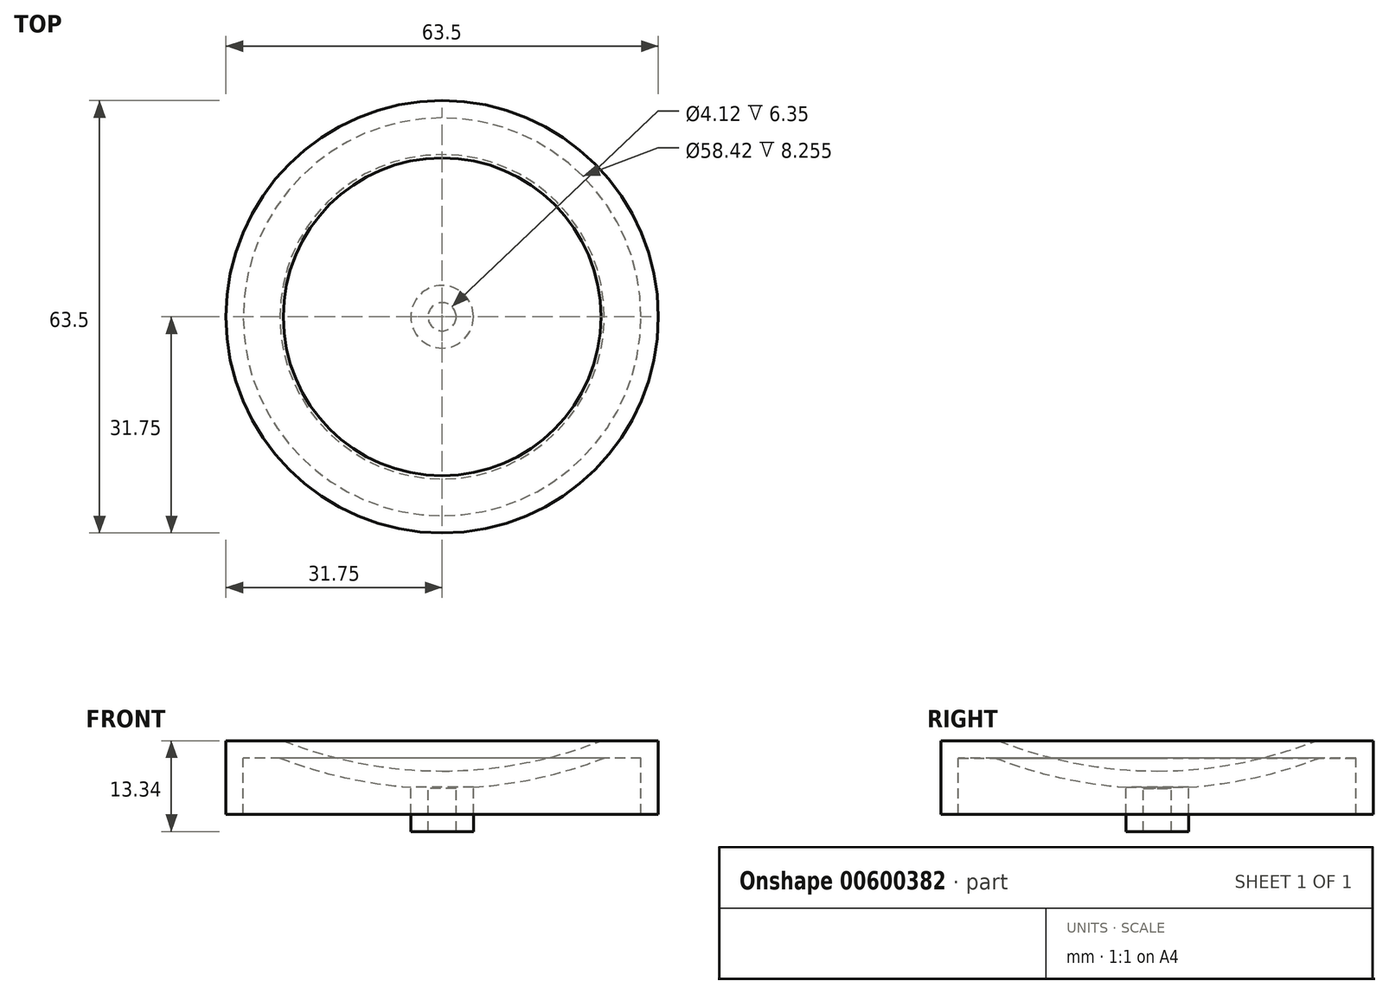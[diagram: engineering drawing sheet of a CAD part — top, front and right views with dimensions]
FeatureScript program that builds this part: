
annotation { "Feature Type Name" : "Feature", "Feature Type Description" : "" }
export const myFeature = defineFeature(function(context is Context, id is Id, definition is map)
    precondition{}
    {
        {
            var Q0;
            Q0=qCreatedBy(makeId("Front.planeOp"),FACE);
            var sketch = newSketch(context, id + "F0", { "sketchPlane" : qUnion([Q0])});
            skCircle(sketch, "E0", {"center": v(0, 59.06) * mm, "radius": 63.5 * mm, "construction": true});
            skLineSegment(sketch, "E1", {"start": v(0, -4.44) * mm, "end": v(0, -6.98) * mm});
            skLineSegment(sketch, "E2", {"start": v(0, -6.98) * mm, "end": v(2.06, -6.98) * mm});
            skLineSegment(sketch, "E3", {"start": v(2.06, -6.98) * mm, "end": v(2.06, -13.33) * mm});
            skLineSegment(sketch, "E4", {"start": v(2.06, -13.33) * mm, "end": v(4.6, -13.33) * mm});
            skLineSegment(sketch, "E5", {"start": v(4.6, -13.33) * mm, "end": v(4.6, -6.82) * mm});
            skLineSegment(sketch, "E6", {"start": v(23.34, 0) * mm, "end": v(31.75, 0) * mm});
            skLineSegment(sketch, "E7", {"start": v(31.75, 0) * mm, "end": v(31.75, -10.8) * mm});
            skLineSegment(sketch, "E8", {"start": v(31.75, -10.8) * mm, "end": v(29.21, -10.8) * mm});
            skLineSegment(sketch, "E9", {"start": v(29.21, -10.8) * mm, "end": v(29.21, -2.54) * mm});
            skLineSegment(sketch, "E10", {"start": v(29.21, -2.54) * mm, "end": v(23.82, -2.54) * mm});
            skArc(sketch, "E11", {"start": v(0, -4.44) * mm, "mid": v(11.88, -3.32) * mm, "end": v(23.34, 0) * mm});
            skArc(sketch, "E12", {"start": v(4.6, -6.82) * mm, "mid": v(14.37, -5.4) * mm, "end": v(23.82, -2.54) * mm});
            skSolve(sketch);
        }
        {
            var Q0;
            Q0=makeQuery(id+"F0.imprint","IMPRINT",FACE,{"disambiguationData":[TD([[makeQuery(id+"F0.imprint","IMPRINT",EDGE,{"derivedFrom":sQuery(id+"F0.wireOp",EDGE,"E1")}),1.0]])]});
            var Q1;
            Q1=sQuery(id+"F0.wireOp",EDGE,"E1");
            revolve(context, id + "F1", {"entities" : qUnion([Q0]), "axis" : qUnion([Q1]), "revolveType" : RevolveType.FULL});
        }
    });
